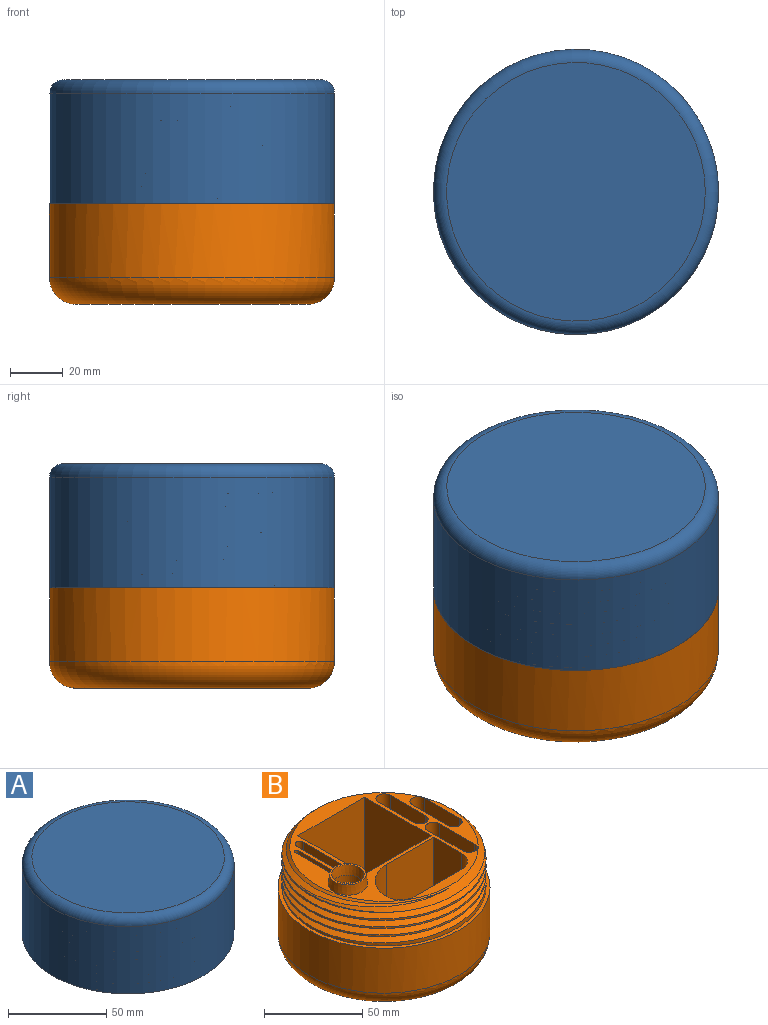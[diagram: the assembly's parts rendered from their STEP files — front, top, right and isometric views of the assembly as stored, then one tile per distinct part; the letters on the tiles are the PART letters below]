
ASSEMBLY  parts=2 mates=1
PART A: 17 faces, bbox 117.9x124.5x50.4 mm
  f0: cylinder r=50mm len=100mm, axis (0,0,-1), area 2514.2mm2, adj f1,f11,f13,f14,f15
  f1: cylinder r=50mm len=100mm, axis (0,0,-1), area 313.5mm2, adj f0,f2,f13,f14
  f2: cylinder r=50mm len=100mm, axis (0,0,-1), area 314.1mm2, adj f1,f3,f13,f14
  f3: cylinder r=50mm len=100mm, axis (0,0,-1), area 314.6mm2, adj f2,f4,f13,f14
  f4: cylinder r=50mm len=100mm, axis (0,0,-1), area 314mm2, adj f3,f5,f13,f14
  f5: cylinder r=50mm len=100mm, axis (0,0,-1), area 314.2mm2, adj f4,f6,f13,f14
  f6: cylinder r=50mm len=100mm, axis (0,0,-1), area 313.8mm2, adj f5,f7,f13,f14
  f7: cylinder r=50mm len=65mm, axis (0,0,-1), area 62.5mm2, adj f6,f12,f13,f14
  f8: cylinder r=54mm len=108mm, axis (0,0,-1), area 14250.3mm2, adj f10,f16
  f9: plane 98x98mm, normal (0,0,1), area 7543mm2, adj f16
  f10: plane 109.02x109.02mm, normal (0,0,-1), area 584.4mm2, adj f8,f12,f13,f14
  f11: plane 100x100mm, normal (0,0,-1), area 7854mm2, adj f0
  f12: cone r=50mm half-angle=45deg, axis (0,0,-1), area 391.7mm2, adj f7,f10,f13,f14
  f13: bspline ~123.47x106.93mm, area 9977.7mm2, adj f0,f1,f2,f3,f4,f5,f6,f7
  f14: bspline ~123.47x106.93mm, area 9476.1mm2, adj f0,f1,f2,f3,f4,f5,f6,f7
  f15: plane 4x3.46mm, normal (0,-1,0), area 6.9mm2, adj f0,f13,f14
  f16: torus R=49mm, axis (0,0,1), area 2575.1mm2, adj f8,f9
PART B: 54 faces, bbox 116.9x120.1x69 mm
  f0: cylinder r=52mm len=104mm, axis (0,0,-1), area 1910.9mm2, adj f46,f47,f48,f49,f51
  f1: plane 96x96mm, normal (0,0,1), area 2073.8mm2, adj f2,f3,f4,f7,f9,f10,f11,f12
  f2: plane 62.5x48mm, normal (-1,0,0), area 2781.3mm2, adj f1,f3,f5,f6,f7,f8
  f3: plane 62.5x48mm, normal (0,-1,0), area 3000mm2, adj f1,f2,f4,f6
  f4: plane 62.5x48mm, normal (1,0,0), area 2781.3mm2, adj f1,f3,f5,f6,f7,f8
  f5: plane 48x17.5mm, normal (0,1,0), area 840mm2, adj f2,f4,f6,f8
  f6: plane 48x35.5mm, normal (0,0,1), area 1704mm2, adj f2,f3,f4,f5
  f7: plane 48x45mm, normal (0,1,0), area 2160mm2, adj f1,f2,f4,f8
  f8: plane 48x12.5mm, normal (0,0,1), area 600mm2, adj f2,f4,f5,f7
  f9: cylinder r=1.25mm len=9.5mm, axis (0,0,1), area 37.3mm2, adj f1,f10,f12,f13
  f10: plane 24x9.5mm, normal (1,0,0), area 228mm2, adj f1,f9,f11,f13
  f11: cylinder r=1.25mm len=9.5mm, axis (0,0,1), area 37.3mm2, adj f1,f10,f12,f13
  f12: plane 24x9.5mm, normal (-1,0,0), area 228mm2, adj f1,f9,f11,f13
  f13: plane 26.5x2.5mm, normal (0,0,1), area 64.9mm2, adj f9,f10,f11,f12
  f14: cylinder r=4.25mm len=17.5mm, axis (0,0,1), area 233.7mm2, adj f1,f15,f17,f18
  f15: plane 25.5x17.5mm, normal (1,0,0), area 446.3mm2, adj f1,f14,f16,f18
  f16: cylinder r=4.25mm len=17.5mm, axis (0,0,1), area 233.7mm2, adj f1,f15,f17,f18
  f17: plane 25.5x17.5mm, normal (-1,0,0), area 446.3mm2, adj f1,f14,f16,f18
  f18: plane 34x8.5mm, normal (0,0,1), area 273.5mm2, adj f14,f15,f16,f17
  f19: cylinder r=4.25mm len=17.5mm, axis (0,0,1), area 233.7mm2, adj f1,f20,f22,f23,f46
  f20: plane 25.5x17.5mm, normal (1,0,0), area 446.3mm2, adj f1,f19,f21,f23
  f21: cylinder r=4.25mm len=17.5mm, axis (0,0,1), area 233.7mm2, adj f1,f20,f22,f23
  f22: plane 25.5x17.5mm, normal (-1,0,0), area 446.3mm2, adj f1,f19,f21,f23
  f23: plane 34x8.5mm, normal (0,0,1), area 273.5mm2, adj f19,f20,f21,f22
  f24: cylinder r=4.25mm len=17.5mm, axis (0,0,1), area 233.7mm2, adj f1,f25,f27,f28
  f25: plane 25.5x17.5mm, normal (1,0,0), area 446.3mm2, adj f1,f24,f26,f28
  f26: cylinder r=4.25mm len=17.5mm, axis (0,0,1), area 233.7mm2, adj f1,f25,f27,f28
  f27: plane 25.5x17.5mm, normal (-1,0,0), area 446.3mm2, adj f1,f24,f26,f28
  f28: plane 34x8.5mm, normal (0,0,1), area 273.5mm2, adj f24,f25,f26,f27
  f29: cylinder r=2.5mm len=18.5mm, axis (0,0,1), area 145.3mm2, adj f1,f30,f32,f33
  f30: plane 30x18.5mm, normal (-1,0,0), area 555mm2, adj f1,f29,f31,f33
  f31: cylinder r=2.5mm len=18.5mm, axis (0,0,1), area 145.3mm2, adj f1,f30,f32,f33
  f32: plane 30x18.5mm, normal (1,0,0), area 555mm2, adj f1,f29,f31,f33
  f33: plane 35x5mm, normal (0,0,1), area 169.6mm2, adj f29,f30,f31,f32
  f34: cone r=7.65mm half-angle=6deg, axis (0,0,1), area 301.9mm2, adj f36,f38
  f35: cone r=10mm half-angle=6deg, axis (0,0,-1), area 367.1mm2, adj f1,f36
  f36: plane 18.74x18.74mm, normal (0,0,1), area 60.4mm2, adj f34,f35
  f37: plane 15.3x15.3mm, normal (0,0,1), area 183.9mm2, adj f38
  f38: cylinder r=7.65mm len=15.3mm, axis (0,0,1), area 216.3mm2, adj f34,f37
  f39: plane 60x20mm, normal (-1,0,0), area 1200mm2, adj f1,f40,f44,f45
  f40: plane 60x34mm, normal (0,-1,0), area 2040mm2, adj f1,f39,f41,f45
  f41: cylinder r=20mm len=60mm, axis (0,0,1), area 1885mm2, adj f1,f40,f42,f45
  f42: cylinder r=10mm len=60mm, axis (0,0,1), area 942.5mm2, adj f1,f41,f43,f45
  f43: plane 60x34mm, normal (0,1,0), area 2040mm2, adj f1,f42,f44,f45
  f44: cylinder r=10mm len=60mm, axis (0,0,1), area 942.5mm2, adj f1,f39,f43,f45
  f45: plane 54x30mm, normal (0,0,1), area 1491.2mm2, adj f39,f40,f41,f42,f43,f44
  f46: cone r=52mm half-angle=45deg, axis (0,0,-1), area 1151mm2, adj f0,f1,f19,f48,f49
  f47: plane 4x3.46mm, normal (-1,0,0), area 6.9mm2, adj f0,f48,f49
  f48: bspline ~120.09x104mm, area 5493.7mm2, adj f0,f46,f47,f49
  f49: bspline ~120.09x104mm, area 4981mm2, adj f0,f46,f47,f48
  f50: cylinder r=54mm len=108mm, axis (0,0,-1), area 9500.2mm2, adj f51,f53
  f51: plane 108x108mm, normal (0,0,1), area 666mm2, adj f0,f50
  f52: plane 88x88mm, normal (0,0,-1), area 6082.1mm2, adj f53
  f53: torus R=44mm, axis (0,0,1), area 4970.9mm2, adj f50,f52
PLACE A t=(-129.23,0,0)mm
PLACE B at identity
MATE cylindrical A.f8 <-> B.f50  axis (0,0,-1) through (0,0,-25)mm
